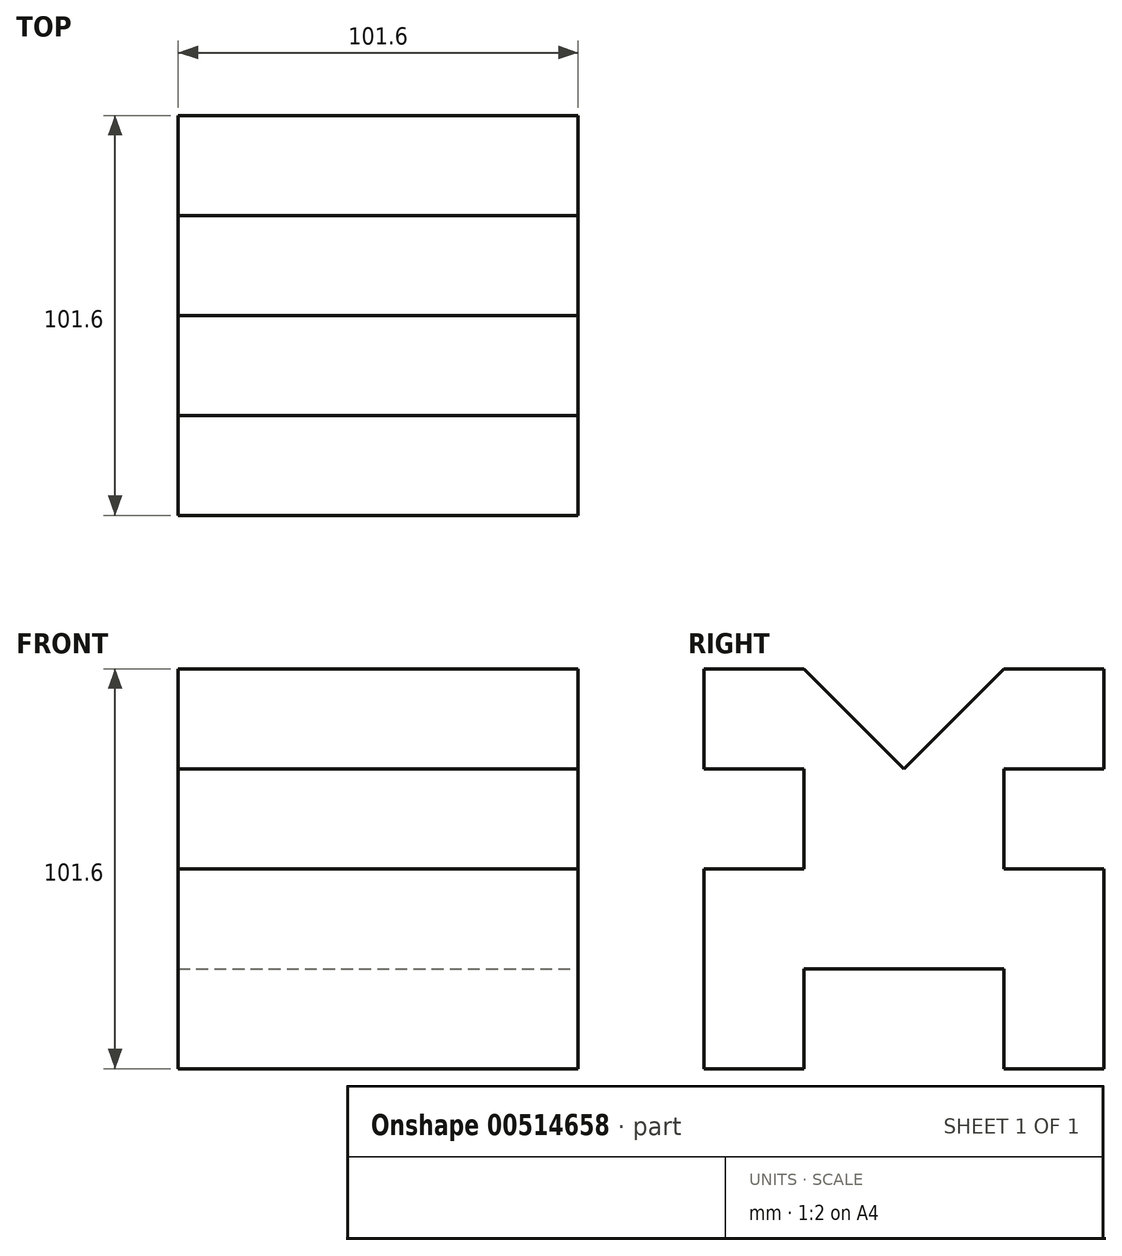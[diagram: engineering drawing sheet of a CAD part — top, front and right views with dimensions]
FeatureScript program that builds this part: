
annotation { "Feature Type Name" : "Feature", "Feature Type Description" : "" }
export const myFeature = defineFeature(function(context is Context, id is Id, definition is map)
    precondition{}
    {
        {
            var Q0;
            Q0=qCreatedBy(makeId("Front.planeOp"),FACE);
            var sketch = newSketch(context, id + "F0", { "sketchPlane" : qUnion([Q0])});
            skLineSegment(sketch, "E0", {"start": v(0, 0) * mm, "end": v(-101.6, 0) * mm});
            skLineSegment(sketch, "E1", {"start": v(0, 0) * mm, "end": v(0, 25.4) * mm});
            skLineSegment(sketch, "E2", {"start": v(0, 25.4) * mm, "end": v(-101.6, 25.4) * mm});
            skLineSegment(sketch, "E3", {"start": v(-101.6, 25.4) * mm, "end": v(-101.6, 0) * mm});
            skLineSegment(sketch, "E4", {"start": v(0, 25.4) * mm, "end": v(0, 50.8) * mm});
            skLineSegment(sketch, "E5", {"start": v(0, 50.8) * mm, "end": v(-101.6, 50.8) * mm});
            skLineSegment(sketch, "E6", {"start": v(-101.6, 50.8) * mm, "end": v(-101.6, 25.4) * mm});
            skLineSegment(sketch, "E7", {"start": v(-101.6, 0) * mm, "end": v(-101.6, -50.8) * mm});
            skLineSegment(sketch, "E8", {"start": v(-101.6, -50.8) * mm, "end": v(0, -50.8) * mm});
            skLineSegment(sketch, "E9", {"start": v(0, -50.8) * mm, "end": v(0, 0) * mm});
            skSolve(sketch);
        }
        {
            var Q0;
            Q0=makeQuery(id+"F0.imprint","IMPRINT",FACE,{"disambiguationData":[TD([[makeQuery(id+"F0.imprint","IMPRINT",EDGE,{"derivedFrom":sQuery(id+"F0.wireOp",EDGE,"E2")}),-1.0]])]});
            var Q1;
            Q1=makeQuery(id+"F0.imprint","IMPRINT",FACE,{"disambiguationData":[TD([[makeQuery(id+"F0.imprint","IMPRINT",EDGE,{"derivedFrom":sQuery(id+"F0.wireOp",EDGE,"E0")}),1.0]])]});
            var Q2;
            Q2=makeQuery(id+"F0.imprint","IMPRINT",FACE,{"disambiguationData":[TD([[makeQuery(id+"F0.imprint","IMPRINT",EDGE,{"derivedFrom":sQuery(id+"F0.wireOp",EDGE,"E0")}),-1.0]])]});
            extrude(context, id + "F1", {"entities" : qUnion([Q0, Q1, Q2]), "depth" : 101.6 * mm, "offsetDistance" : 25.4 * mm});
        }
        {
            var Q0;
            Q0=makeQuery(id+"F1.opExtrude","CAP_FACE",FACE,{"disambiguationData":[OSD([sQuery(id+"F0.wireOp",EDGE,"E1"),sQuery(id+"F0.wireOp",EDGE,"E3"),sQuery(id+"F0.wireOp",EDGE,"E4"),sQuery(id+"F0.wireOp",EDGE,"E5"),sQuery(id+"F0.wireOp",EDGE,"E6"),sQuery(id+"F0.wireOp",EDGE,"E7"),sQuery(id+"F0.wireOp",EDGE,"E8"),sQuery(id+"F0.wireOp",EDGE,"E9")])],"isStart":false});
            var sketch = newSketch(context, id + "F2", { "sketchPlane" : qUnion([Q0])});
            skLineSegment(sketch, "E10", {"start": v(0, 0) * mm, "end": v(-101.6, 0) * mm});
            skLineSegment(sketch, "E11", {"start": v(-101.6, 0) * mm, "end": v(-101.6, 25.4) * mm});
            skLineSegment(sketch, "E12", {"start": v(-101.6, 25.4) * mm, "end": v(0, 25.4) * mm});
            skLineSegment(sketch, "E13", {"start": v(0, 25.4) * mm, "end": v(0, 0) * mm});
            skSolve(sketch);
        }
        {
            var Q0;
            Q0=makeQuery(id+"F2.imprint","IMPRINT",FACE,{"disambiguationData":[TD([[makeQuery(id+"F2.imprint","IMPRINT",EDGE,{"derivedFrom":sQuery(id+"F2.wireOp",EDGE,"E10")}),-1.0]])]});
            extrude(context, id + "F3", {"entities" : qUnion([Q0]), "operationType" : NewBodyOperationType.REMOVE, "oppositeDirection" : true, "depth" : 25.4 * mm, "offsetDistance" : 25.4 * mm});
        }
        {
            var Q0;
            Q0=makeQuery(id+"F1.opExtrude","SWEPT_FACE",FACE,{"disambiguationData":[OSD([sQuery(id+"F0.wireOp",EDGE,"E1"),sQuery(id+"F0.wireOp",EDGE,"E4"),sQuery(id+"F0.wireOp",EDGE,"E9")])]});
            var sketch = newSketch(context, id + "F4", { "sketchPlane" : qUnion([Q0])});
            skLineSegment(sketch, "E14", {"start": v(-101.6, -50.8) * mm, "end": v(-76.2, -50.8) * mm});
            skLineSegment(sketch, "E15", {"start": v(-76.2, -50.8) * mm, "end": v(-76.2, -25.4) * mm});
            skLineSegment(sketch, "E16", {"start": v(-76.2, -25.4) * mm, "end": v(-25.4, -25.4) * mm});
            skLineSegment(sketch, "E17", {"start": v(-25.4, -25.4) * mm, "end": v(-25.4, -50.8) * mm});
            skLineSegment(sketch, "E18", {"start": v(-25.4, -50.8) * mm, "end": v(0, -50.8) * mm});
            skSolve(sketch);
        }
        {
            var Q0;
            {var subQ0=sQuery(id+"F4.wireOp",EDGE,"E15");Q0=makeQuery(id+"F4.imprint","IMPRINT",FACE,{"disambiguationData":[TD([[makeQuery(id+"F4.imprint","IMPRINT",EDGE,{"derivedFrom":subQ0}),-1.0]])]});}
            extrude(context, id + "F5", {"entities" : qUnion([Q0]), "operationType" : NewBodyOperationType.REMOVE, "oppositeDirection" : true, "depth" : 101.6 * mm, "offsetDistance" : 25.4 * mm});
        }
        {
            var Q0;
            Q0=makeQuery(id+"F1.opExtrude","SWEPT_FACE",FACE,{"disambiguationData":[OSD([sQuery(id+"F0.wireOp",EDGE,"E1"),sQuery(id+"F0.wireOp",EDGE,"E4"),sQuery(id+"F0.wireOp",EDGE,"E9")])]});
            var sketch = newSketch(context, id + "F6", { "sketchPlane" : qUnion([Q0])});
            skLineSegment(sketch, "E19", {"start": v(0, 0) * mm, "end": v(-25.4, 0) * mm});
            skLineSegment(sketch, "E20", {"start": v(-25.4, 0) * mm, "end": v(-25.4, 25.4) * mm});
            skLineSegment(sketch, "E21", {"start": v(-25.4, 25.4) * mm, "end": v(0, 25.4) * mm});
            skSolve(sketch);
        }
        {
            var Q0;
            {var subQ0=sQuery(id+"F6.wireOp",EDGE,"E19");Q0=makeQuery(id+"F6.imprint","IMPRINT",FACE,{"disambiguationData":[TD([[makeQuery(id+"F6.imprint","IMPRINT",EDGE,{"derivedFrom":subQ0}),-1.0]])]});}
            extrude(context, id + "F7", {"entities" : qUnion([Q0]), "operationType" : NewBodyOperationType.REMOVE, "oppositeDirection" : true, "depth" : 101.6 * mm, "offsetDistance" : 25.4 * mm});
        }
        {
            var Q0;
            Q0=makeQuery(id+"F1.opExtrude","SWEPT_FACE",FACE,{"disambiguationData":[OSD([sQuery(id+"F0.wireOp",EDGE,"E1"),sQuery(id+"F0.wireOp",EDGE,"E4"),sQuery(id+"F0.wireOp",EDGE,"E9")])]});
            var sketch = newSketch(context, id + "F8", { "sketchPlane" : qUnion([Q0])});
            skLineSegment(sketch, "E22", {"start": v(-101.6, 50.8) * mm, "end": v(-76.2, 50.8) * mm});
            skLineSegment(sketch, "E23", {"start": v(-76.2, 25.4) * mm, "end": v(-25.4, 25.4) * mm});
            skLineSegment(sketch, "E24", {"start": v(-76.2, 25.4) * mm, "end": v(-50.8, 25.4) * mm});
            skLineSegment(sketch, "E25", {"start": v(-76.2, 50.8) * mm, "end": v(-50.8, 25.4) * mm});
            skLineSegment(sketch, "E26", {"start": v(0, 50.8) * mm, "end": v(-25.4, 50.8) * mm});
            skLineSegment(sketch, "E27", {"start": v(-25.4, 50.8) * mm, "end": v(-50.8, 25.4) * mm});
            skLineSegment(sketch, "E28", {"start": v(-76.2, 50.8) * mm, "end": v(-25.4, 50.8) * mm});
            skSolve(sketch);
        }
        {
            var Q0;
            Q0=makeQuery(id+"F8.imprint","IMPRINT",FACE,{"disambiguationData":[TD([[makeQuery(id+"F8.imprint","IMPRINT",EDGE,{"derivedFrom":sQuery(id+"F8.wireOp",EDGE,"E25")}),1.0]])]});
            extrude(context, id + "F9", {"entities" : qUnion([Q0]), "operationType" : NewBodyOperationType.REMOVE, "oppositeDirection" : true, "depth" : 101.6 * mm, "offsetDistance" : 25.4 * mm});
        }
    });
